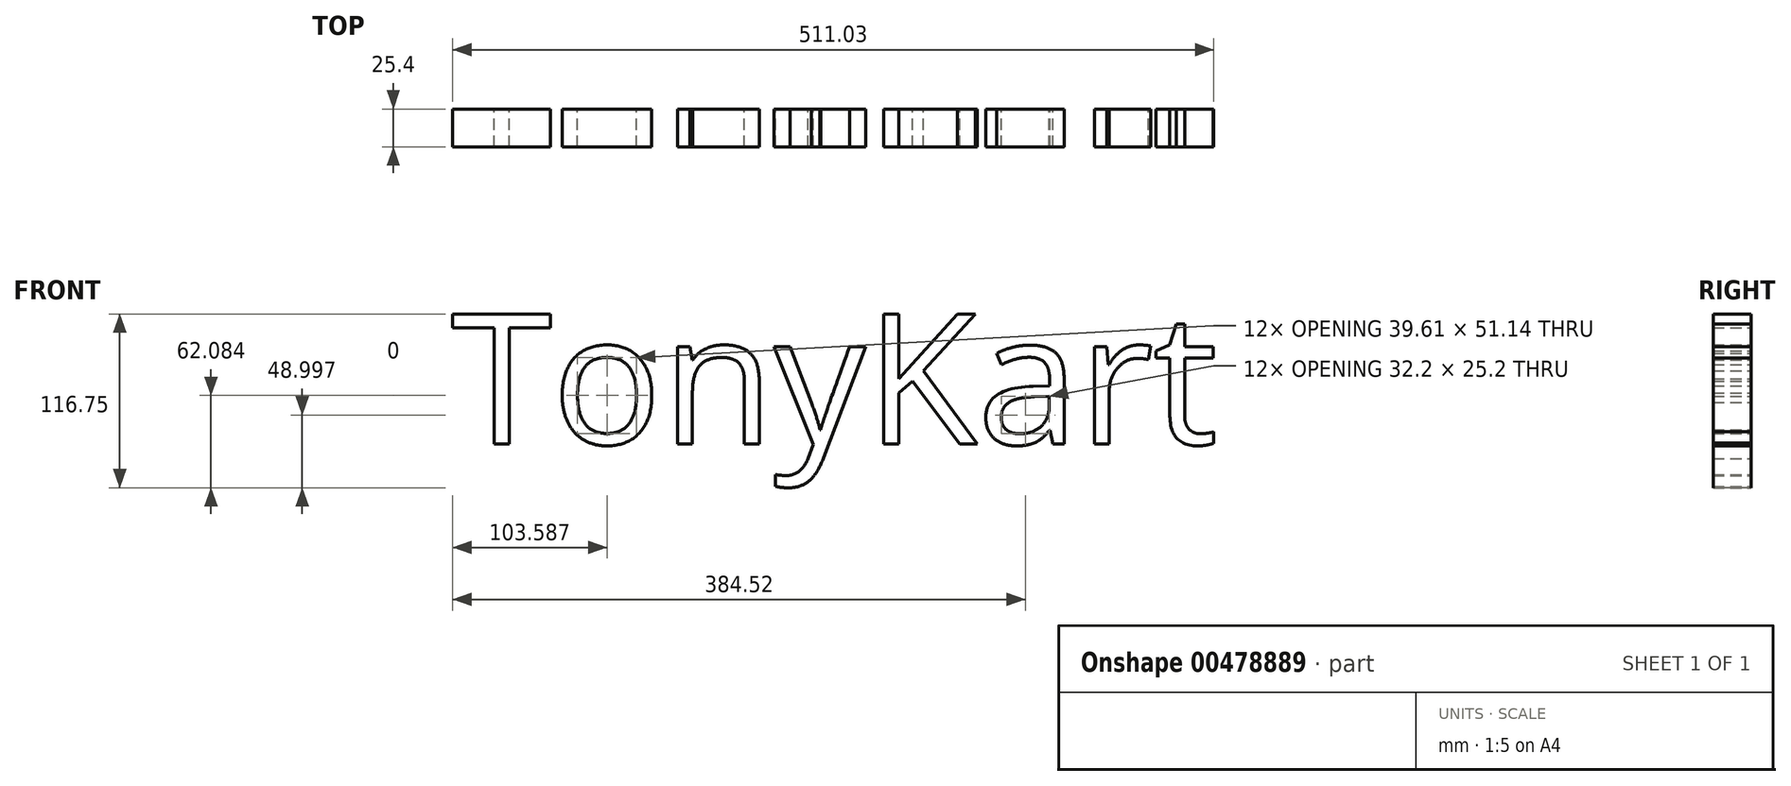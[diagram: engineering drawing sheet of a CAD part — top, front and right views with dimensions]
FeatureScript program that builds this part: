
annotation { "Feature Type Name" : "Feature", "Feature Type Description" : "" }
export const myFeature = defineFeature(function(context is Context, id is Id, definition is map)
    precondition{}
    {
        {
            var Q0;
            Q0=qCreatedBy(makeId("Front.planeOp"),FACE);
            var sketch = newSketch(context, id + "F0", { "sketchPlane" : qUnion([Q0])});
            skText(sketch, "E0", { "text": "TonyKart", "fontName": "OpenSans-Regular.ttf"});
            const initialGuessF0  = {"E0": [-0.43896, -0.03874, 1, 0, 0.0881]};
            skSetInitialGuess(sketch, initialGuessF0);
            skSolve(sketch);
        }
        {
            var Q0;
            Q0=makeQuery(id+"F0.imprint","IMPRINT",FACE,{"disambiguationData":[TD([[makeQuery(id+"F0.imprint","IMPRINT",EDGE,{"derivedFrom":sQuery(id+"F0.wireOp",EDGE,"E0.sketch_text.stroke-0")}),-1.0]])]});
            var Q1;
            Q1=makeQuery(id+"F0.imprint","IMPRINT",FACE,{"disambiguationData":[TD([[makeQuery(id+"F0.imprint","IMPRINT",EDGE,{"derivedFrom":sQuery(id+"F0.wireOp",EDGE,"E0.sketch_text.stroke-8")}),-1.0]])]});
            var Q2;
            Q2=makeQuery(id+"F0.imprint","IMPRINT",FACE,{"disambiguationData":[TD([[makeQuery(id+"F0.imprint","IMPRINT",EDGE,{"derivedFrom":sQuery(id+"F0.wireOp",EDGE,"E0.sketch_text.stroke-25")}),-1.0]])]});
            var Q3;
            Q3=makeQuery(id+"F0.imprint","IMPRINT",FACE,{"disambiguationData":[TD([[makeQuery(id+"F0.imprint","IMPRINT",EDGE,{"derivedFrom":sQuery(id+"F0.wireOp",EDGE,"E0.sketch_text.stroke-42")}),-1.0]])]});
            var Q4;
            Q4=makeQuery(id+"F0.imprint","IMPRINT",FACE,{"disambiguationData":[TD([[makeQuery(id+"F0.imprint","IMPRINT",EDGE,{"derivedFrom":sQuery(id+"F0.wireOp",EDGE,"E0.sketch_text.stroke-97")}),-1.0]])]});
            var Q5;
            Q5=makeQuery(id+"F0.imprint","IMPRINT",FACE,{"disambiguationData":[TD([[makeQuery(id+"F0.imprint","IMPRINT",EDGE,{"derivedFrom":sQuery(id+"F0.wireOp",EDGE,"E0.sketch_text.stroke-70")}),-1.0]])]});
            var Q6;
            Q6=makeQuery(id+"F0.imprint","IMPRINT",FACE,{"disambiguationData":[TD([[makeQuery(id+"F0.imprint","IMPRINT",EDGE,{"derivedFrom":sQuery(id+"F0.wireOp",EDGE,"E0.sketch_text.stroke-58")}),-1.0]])]});
            var Q7;
            Q7=makeQuery(id+"F0.imprint","IMPRINT",FACE,{"disambiguationData":[TD([[makeQuery(id+"F0.imprint","IMPRINT",EDGE,{"derivedFrom":sQuery(id+"F0.wireOp",EDGE,"E0.sketch_text.stroke-110")}),-1.0]])]});
            extrude(context, id + "F1", {"entities" : qUnion([Q0, Q1, Q2, Q3, Q4, Q5, Q6, Q7]), "depth" : 25.4 * mm});
        }
    });
